# Revit family: IS_Contour21_S3126_BIM_DE
name_source: partatom
category: Plumbing Fixtures
revit_build: Autodesk Revit MEP 2016 (Build: 20161004_0715(x64)
units: mm (PartAtom-declared; Revit-internal decimal feet)

## family parameters
Always vertical = No
Cut with Voids When Loaded = No
OmniClass Number = 23.45.05.21.11.11
OmniClass Title = Water Operated Water Closets
Part Type = Normal
Room Calculation Point = No
Round Connector Dimension = Use Diameter
Shared = No
Work Plane-Based = No

## types (2) — shared parameters
Accessories = www.idealstandard.de\ersatzteile
AssetType = Fixed
BIMobject category = Toilets
BOSUseNativeGeometries = 1
Brand = Ideal Standard
Brand url = http://www.idealstandard.de
ConnectionType = Plumbing
CurrencyUnit = €
CurrentRevision = 1
DurationUnit = Jaar
Edition number = 1
ExpectedLife = 25
Features = CONTOUR21 floor standing bowl 360x520mm, wash-down, rimless
IFC Classification = Sanitary Terminal
IfcExportAs = Sanitary terminal type
IfcExportType = TOILET
Installation instructions = http://www.idealstandard.de
InstallationInstructions = www.idealstandard.de\produkte
LinearUnits = millimetres
MaintenanceInformation = www.idealstandard.de
Manufacturer = http://www.idealstandard.de
Manufacturer name = Ideal Standard
ManufacturerURL = http://www.idealstandard.de
Material = Vitreous china
Material main = Ceramics
NettWeight = 19,6 kg
Nominal height = 360
Nominal width = 360
NominalHeight = 401 mm
NominalLength = 522 mm
NominalWidth = 362 mm
Product Guid = 3418fe93-f968-4e29-8f76-87cf54a09771
Product SKU = S3126
Product data url = https://bimobject.com
Product family = CONTOUR 21
Product group = Bowl
Product name = CONTOUR21 floor standing bowl 360x520mm, wash-down, rimless
Product url = http://www.idealstandard.de
ProductInformation = www.idealstandard.de/produkte
QR code = http://bimobject.com
Shape = Sculptured
Size = 401 x 522 x 362mm
Space = Internal
SpareParts = www.idealstandard.de/ersatzteile
Technical description = http://www.idealstandard.de
ToiletPanType = WashDown
ToiletType = Other
URL = http://www.idealstandard.de
Uniclass2015Code = Pr_40_20_93_94
Uniclass2015Title = WC pans
Uniclass2015Version = Products v1.1
VolumeUnits = Litres
Weight Net (Kg) = 19.6
zero-valued in all types: Cost, InletConnectionSize, OutletConnectionSize, SpilloverLevel

## per-type parameters (varying)
| type | BIMObjectName | BarCode | CodePerformance | Color | Description | EAN code | Finish | MainColor | Model | ModelNumber | ModelReference | Name | Product certification |
| S312601 - CONTOUR21 floor standing bowl 360x520mm, wash-down, rimless | ISI_IdealStandard_WCPans_CONTOUR21_S312601 | 5017830466727 | DIN EN 997 | White | S312601 CONTOUR21 floor standing bowl 360x520mm, wash-down, rimless | https://5017830466727 | White | White | S312601 | S312601 | S312601 CONTOUR21 floor standing bowl 360x520mm, wash-down, rimless | ISI_IdealStandard_WCPans_CONTOUR21_S312601 | DIN EN 997 |
| S3126MA - CONTOUR21 floor standing bowl 360x520mm, wash-down, rimless | ISI_IdealStandard_WCPans_CONTOUR21_S3126MA | 5017830476559 | 0 | WHITE IP | S3126MA CONTOUR21 floor standing bowl 360x520mm, wash-down, rimless | https://5017830476559 | WHITE IP | WHITE IP | S3126MA | S3126MA | S3126MA CONTOUR21 floor standing bowl 360x520mm, wash-down, rimless | ISI_IdealStandard_WCPans_CONTOUR21_S3126MA | 0 |

## geometry (parser evidence)
native form markers: Blend x2, Sweep x3
no freeform markers — native parametric forms only
